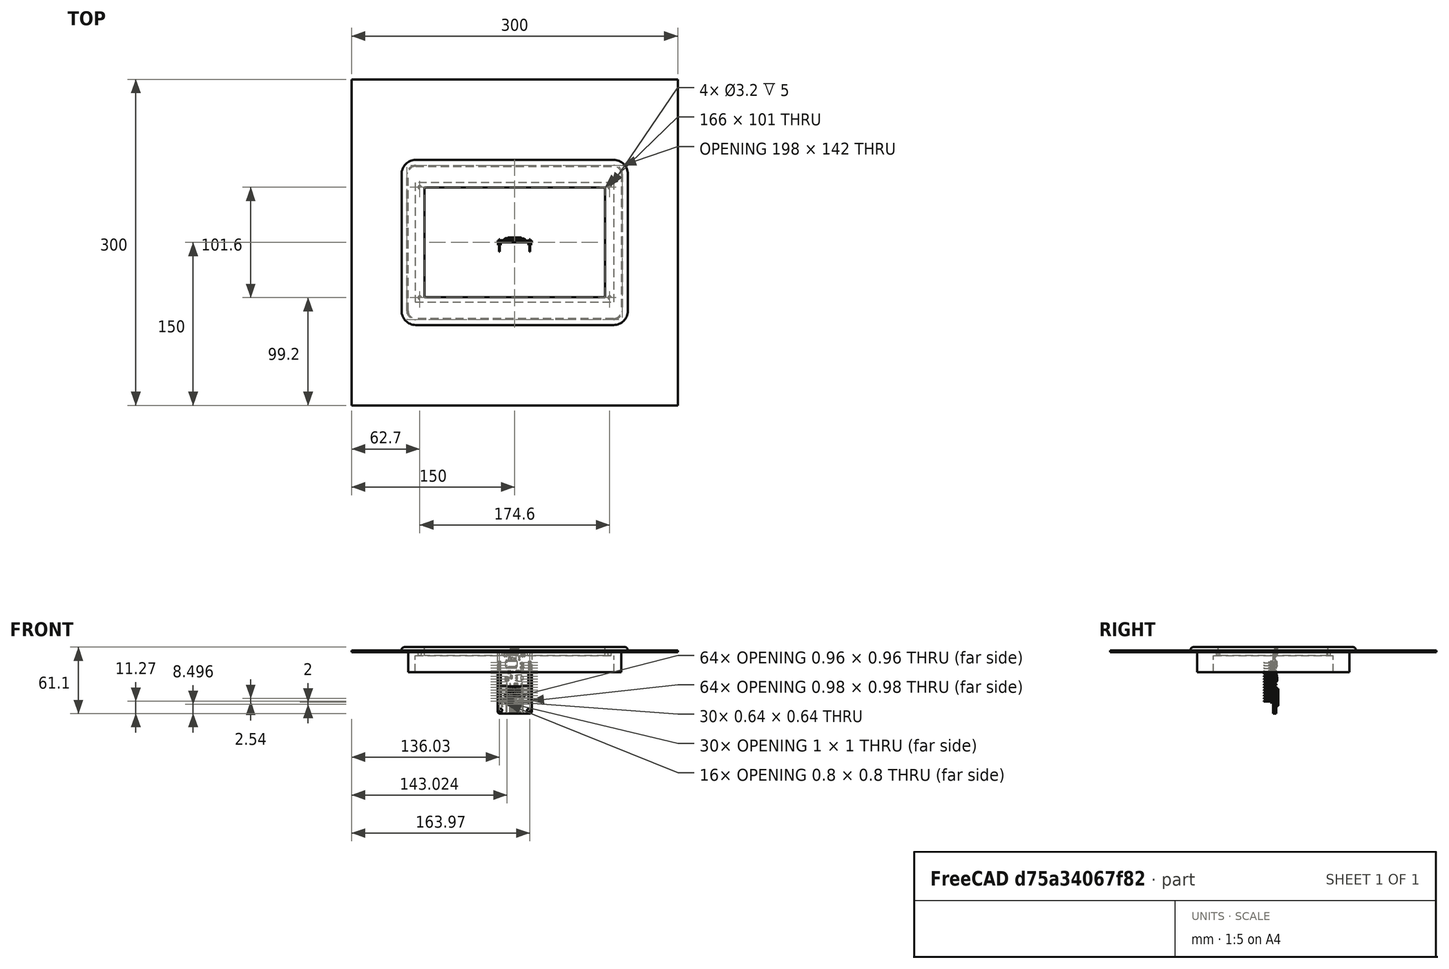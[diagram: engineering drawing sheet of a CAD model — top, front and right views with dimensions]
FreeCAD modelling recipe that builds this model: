
FCSTD DOCUMENT  (FreeCAD 0.19R21718 (Git))
Label: Marco_Respirator_2020
License: All rights reserved
LicenseURL: http://en.wikipedia.org/wiki/All_rights_reserved
objects: Sketcher::SketchObject×8, PartDesign::Pocket×4, PartDesign::Pad×3, PartDesign::Body×2, Part::Feature×2, PartDesign::Fillet×1, Mesh::Feature×1, App::Part×1
note: 28 computed .brp shape members not serialized (recipe doc carries the construction recipe); baked Part::Feature solids carry a one-line shape summary decoded from their .brp

FEATURE [Sketcher::SketchObject] Sketch
  MapMode = 5
  Support = -> [XY_Plane]
  sketch-geometry (4):
    g0: LineSegment StartX=-150 StartY=150 StartZ=0 EndX=150 EndY=150 EndZ=0
    g1: LineSegment StartX=150 StartY=150 StartZ=0 EndX=150 EndY=-150 EndZ=0
    g2: LineSegment StartX=150 StartY=-150 StartZ=0 EndX=-150 EndY=-150 EndZ=0
    g3: LineSegment StartX=-150 StartY=-150 StartZ=0 EndX=-150 EndY=150 EndZ=0
  constraints (11):
    c: Coincident(g0,g1)
    c: Coincident(g1,g2)
    c: Coincident(g2,g3)
    c: Coincident(g3,g0)
    c: Horizontal(g0)
    c: Horizontal(g2)
    c: Vertical(g1)
    c: Vertical(g3)
    c: DistanceY(g1,g1) = 300
    c: DistanceX(g2,g2) = 300
    c: Symmetric(g2,g0,g-1)
FEATURE [PartDesign::Pad] Pad
  Length = 1.5
  Length2 = 100
  Profile = -> Sketch
  Type = 0
FEATURE [Sketcher::SketchObject] Sketch001
  MapMode = 5
  Support = -> [XY_Plane]
  sketch-geometry (8):
    g0: LineSegment StartX=-91 StartY=71 StartZ=0 EndX=91 EndY=71 EndZ=0
    g1: LineSegment StartX=99 StartY=63 StartZ=0 EndX=99 EndY=-63 EndZ=0
    g2: LineSegment StartX=91 StartY=-71 StartZ=0 EndX=-91 EndY=-71 EndZ=0
    g3: LineSegment StartX=-99 StartY=-63 StartZ=0 EndX=-99 EndY=63 EndZ=0
    g4: ArcOfCircle CenterX=-91 CenterY=63 CenterZ=0 NormalX=0 NormalY=0 NormalZ=1 AngleXU=0 Radius=8 StartAngle=1.5708 EndAngle=3.14159
    g5: ArcOfCircle CenterX=91 CenterY=63 CenterZ=0 NormalX=0 NormalY=0 NormalZ=1 AngleXU=0 Radius=8 StartAngle=-5.87e-12 EndAngle=1.5708
    g6: ArcOfCircle CenterX=91 CenterY=-63 CenterZ=0 NormalX=0 NormalY=0 NormalZ=1 AngleXU=0 Radius=8 StartAngle=4.71239 EndAngle=6.28319
    g7: ArcOfCircle CenterX=-91 CenterY=-63 CenterZ=0 NormalX=0 NormalY=0 NormalZ=1 AngleXU=0 Radius=8 StartAngle=3.14159 EndAngle=4.71239
  constraints (19):
    c: Horizontal(g0)
    c: Horizontal(g2)
    c: Vertical(g1)
    c: Vertical(g3)
    c: Tangent(g3,g4) = 1.5708
    c: Tangent(g0,g4) = 1.5708
    c: Tangent(g0,g5) = 1.5708
    c: Tangent(g1,g5) = 1.5708
    c: Tangent(g1,g6) = 1.5708
    c: Tangent(g2,g6) = 1.5708
    c: Tangent(g2,g7) = 1.5708
    c: Tangent(g3,g7) = 1.5708
    c: Radius(g4) = 8
    c: Equal(g4,g5)
    c: Equal(g4,g6)
    c: Equal(g4,g7)
    c: Symmetric(g7,g5,g-1)
    c: DistanceX(g3,g1) = 198
    c: DistanceY(g2,g0) = 142
FEATURE [PartDesign::Pocket] Pocket
  BaseFeature = -> Pad
  Length = 5
  Length2 = 100
  Profile = -> Sketch001
  Reversed = true
  Type = 1
FEATURE [PartDesign::Body] Body  label="Chapa_Exterior"
  Group = -> [Sketch,Pad,Sketch001,Pocket]
  Origin = -> Origin
  Placement = pos=(0,0,-1.5) rot=(0,0,1;0rad)
  Tip = -> Pocket
FEATURE [Sketcher::SketchObject] Sketch002
  MapMode = 5
  Support = -> [XY_Plane001]
  expr: Constraints[12] = Sketch003.Constraints[12]
  expr: Constraints[17] = Sketch003.Constraints[17]
  expr: .Constraints.Ancho = Sketch003.Constraints[18]
  expr: Constraints[34] = .Constraints.Ancho + 10mm
  sketch-geometry (16):
    g0: LineSegment [constr] StartX=-91 StartY=71 StartZ=0 EndX=91 EndY=71 EndZ=0
    g1: LineSegment [constr] StartX=99 StartY=63 StartZ=0 EndX=99 EndY=-63 EndZ=0
    g2: LineSegment [constr] StartX=91 StartY=-71 StartZ=0 EndX=-91 EndY=-71 EndZ=0
    g3: LineSegment [constr] StartX=-99 StartY=-63 StartZ=0 EndX=-99 EndY=63 EndZ=0
    g4: ArcOfCircle [constr] CenterX=-91 CenterY=63 CenterZ=0 NormalX=0 NormalY=0 NormalZ=1 AngleXU=0 Radius=8 StartAngle=1.5708 EndAngle=3.14159
    g5: ArcOfCircle [constr] CenterX=91 CenterY=63 CenterZ=0 NormalX=0 NormalY=0 NormalZ=1 AngleXU=0 Radius=8 StartAngle=1e-16 EndAngle=1.5708
    g6: ArcOfCircle [constr] CenterX=91 CenterY=-63 CenterZ=0 NormalX=0 NormalY=0 NormalZ=1 AngleXU=0 Radius=8 StartAngle=4.71239 EndAngle=6.28319
    g7: ArcOfCircle [constr] CenterX=-91 CenterY=-63 CenterZ=0 NormalX=0 NormalY=0 NormalZ=1 AngleXU=0 Radius=8 StartAngle=3.14159 EndAngle=4.71239
    g8: LineSegment StartX=-91 StartY=76 StartZ=0 EndX=91 EndY=76 EndZ=0
    g9: LineSegment StartX=104 StartY=63 StartZ=0 EndX=104 EndY=-63 EndZ=0
    g10: LineSegment StartX=91 StartY=-76 StartZ=0 EndX=-91 EndY=-76 EndZ=0
    g11: LineSegment StartX=-104 StartY=-63 StartZ=0 EndX=-104 EndY=63 EndZ=0
    g12: ArcOfCircle CenterX=-91 CenterY=63 CenterZ=0 NormalX=0 NormalY=0 NormalZ=1 AngleXU=0 Radius=13 StartAngle=1.5708 EndAngle=3.14159
    g13: ArcOfCircle CenterX=91 CenterY=63 CenterZ=0 NormalX=0 NormalY=0 NormalZ=1 AngleXU=0 Radius=13 StartAngle=4e-15 EndAngle=1.5708
    g14: ArcOfCircle CenterX=91 CenterY=-63 CenterZ=0 NormalX=0 NormalY=0 NormalZ=1 AngleXU=0 Radius=13 StartAngle=4.71239 EndAngle=6.28319
    g15: ArcOfCircle CenterX=-91 CenterY=-63 CenterZ=0 NormalX=0 NormalY=0 NormalZ=1 AngleXU=0 Radius=13 StartAngle=3.14159 EndAngle=4.71239
  constraints (35):
    c: Horizontal(g0)
    c: Horizontal(g2)
    c: Vertical(g1)
    c: Vertical(g3)
    c: Tangent(g3,g4) = 1.5708
    c: Tangent(g0,g4) = 1.5708
    c: Tangent(g0,g5) = 1.5708
    c: Tangent(g1,g5) = 1.5708
    c: Tangent(g1,g6) = 1.5708
    c: Tangent(g2,g6) = 1.5708
    c: Tangent(g2,g7) = 1.5708
    c: Tangent(g3,g7) = 1.5708
    c: Radius(g4) = 8
    c: Equal(g4,g5)
    c: Equal(g4,g6)
    c: Equal(g4,g7)
    c: Symmetric(g7,g5,g-1)
    c: DistanceX(g3,g1) = 198
    c: DistanceY(g2,g0) = 142  'Ancho'
    c: Horizontal(g8)
    c: Horizontal(g10)
    c: Vertical(g9)
    c: Tangent(g11,g12) = 1.5708
    c: Tangent(g8,g12) = 1.5708
    c: Tangent(g8,g13) = 1.5708
    c: Tangent(g9,g13) = 1.5708
    c: Tangent(g9,g14) = 1.5708
    c: Tangent(g10,g14) = 1.5708
    c: Tangent(g10,g15) = 1.5708
    c: Tangent(g11,g15) = 1.5708
    c: Coincident(g12,g4)
    c: Coincident(g13,g5)
    c: Coincident(g14,g6)
    c: Coincident(g15,g7)
    c: DistanceY(g10,g8) = 152
FEATURE [Sketcher::SketchObject] Sketch003
  MapMode = 5
  Support = -> [XY_Plane001]
  sketch-geometry (8):
    g0: LineSegment StartX=-91 StartY=71 StartZ=0 EndX=91 EndY=71 EndZ=0
    g1: LineSegment StartX=99 StartY=63 StartZ=0 EndX=99 EndY=-63 EndZ=0
    g2: LineSegment StartX=91 StartY=-71 StartZ=0 EndX=-91 EndY=-71 EndZ=0
    g3: LineSegment StartX=-99 StartY=-63 StartZ=0 EndX=-99 EndY=63 EndZ=0
    g4: ArcOfCircle CenterX=-91 CenterY=63 CenterZ=0 NormalX=0 NormalY=0 NormalZ=1 AngleXU=0 Radius=8 StartAngle=1.5708 EndAngle=3.14159
    g5: ArcOfCircle CenterX=91 CenterY=63 CenterZ=0 NormalX=0 NormalY=0 NormalZ=1 AngleXU=0 Radius=8 StartAngle=-5.87e-12 EndAngle=1.5708
    g6: ArcOfCircle CenterX=91 CenterY=-63 CenterZ=0 NormalX=0 NormalY=0 NormalZ=1 AngleXU=0 Radius=8 StartAngle=4.71239 EndAngle=6.28319
    g7: ArcOfCircle CenterX=-91 CenterY=-63 CenterZ=0 NormalX=0 NormalY=0 NormalZ=1 AngleXU=0 Radius=8 StartAngle=3.14159 EndAngle=4.71239
  constraints (19):
    c: Horizontal(g0)
    c: Horizontal(g2)
    c: Vertical(g1)
    c: Vertical(g3)
    c: Tangent(g3,g4) = 1.5708
    c: Tangent(g0,g4) = 1.5708
    c: Tangent(g0,g5) = 1.5708
    c: Tangent(g1,g5) = 1.5708
    c: Tangent(g1,g6) = 1.5708
    c: Tangent(g2,g6) = 1.5708
    c: Tangent(g2,g7) = 1.5708
    c: Tangent(g3,g7) = 1.5708
    c: Radius(g4) = 8
    c: Equal(g4,g5)
    c: Equal(g4,g6)
    c: Equal(g4,g7)
    c: Symmetric(g7,g5,g-1)
    c: DistanceX(g3,g1) = 198
    c: DistanceY(g2,g0) = 142
FEATURE [PartDesign::Pad] Pad001
  Length = 3
  Length2 = 100
  Profile = -> Sketch002
  Type = 0
FEATURE [Sketcher::SketchObject] Sketch004
  MapMode = 5
  Support = -> [XY_Plane001]
  expr: Constraints[12] = Sketch003.Constraints[12]
  expr: Constraints[17] = Sketch003.Constraints[17]
  expr: .Constraints.Ancho = Sketch003.Constraints[18]
  expr: Constraints[34] = .Constraints.Ancho - 2mm
  sketch-geometry (16):
    g0: LineSegment [constr] StartX=-91 StartY=71 StartZ=0 EndX=91 EndY=71 EndZ=0
    g1: LineSegment [constr] StartX=99 StartY=63 StartZ=0 EndX=99 EndY=-63 EndZ=0
    g2: LineSegment [constr] StartX=91 StartY=-71 StartZ=0 EndX=-91 EndY=-71 EndZ=0
    g3: LineSegment [constr] StartX=-99 StartY=-63 StartZ=0 EndX=-99 EndY=63 EndZ=0
    g4: ArcOfCircle [constr] CenterX=-91 CenterY=63 CenterZ=0 NormalX=0 NormalY=0 NormalZ=1 AngleXU=0 Radius=8 StartAngle=1.5708 EndAngle=3.14159
    g5: ArcOfCircle [constr] CenterX=91 CenterY=63 CenterZ=0 NormalX=0 NormalY=0 NormalZ=1 AngleXU=0 Radius=8 StartAngle=-9e-16 EndAngle=1.5708
    g6: ArcOfCircle [constr] CenterX=91 CenterY=-63 CenterZ=0 NormalX=0 NormalY=0 NormalZ=1 AngleXU=0 Radius=8 StartAngle=4.71239 EndAngle=6.28319
    g7: ArcOfCircle [constr] CenterX=-91 CenterY=-63 CenterZ=0 NormalX=0 NormalY=0 NormalZ=1 AngleXU=0 Radius=8 StartAngle=3.14159 EndAngle=4.71239
    g8: LineSegment StartX=-91 StartY=70 StartZ=0 EndX=91 EndY=70 EndZ=0
    g9: LineSegment StartX=98 StartY=63 StartZ=0 EndX=98 EndY=-63 EndZ=0
    g10: LineSegment StartX=91 StartY=-70 StartZ=0 EndX=-91 EndY=-70 EndZ=0
    g11: LineSegment StartX=-98 StartY=-63 StartZ=0 EndX=-98 EndY=63 EndZ=0
    g12: ArcOfCircle CenterX=91 CenterY=-63 CenterZ=0 NormalX=0 NormalY=0 NormalZ=1 AngleXU=0 Radius=7 StartAngle=4.71239 EndAngle=6.28319
    g13: ArcOfCircle CenterX=-91 CenterY=-63 CenterZ=0 NormalX=0 NormalY=0 NormalZ=1 AngleXU=0 Radius=7 StartAngle=3.14159 EndAngle=4.71239
    g14: ArcOfCircle CenterX=-91 CenterY=63 CenterZ=0 NormalX=0 NormalY=0 NormalZ=1 AngleXU=0 Radius=7 StartAngle=1.5708 EndAngle=3.14159
    g15: ArcOfCircle CenterX=91 CenterY=63 CenterZ=0 NormalX=0 NormalY=0 NormalZ=1 AngleXU=0 Radius=7 StartAngle=2e-16 EndAngle=1.5708
  constraints (35):
    c: Horizontal(g0)
    c: Horizontal(g2)
    c: Vertical(g1)
    c: Vertical(g3)
    c: Tangent(g3,g4) = 1.5708
    c: Tangent(g0,g4) = 1.5708
    c: Tangent(g0,g5) = 1.5708
    c: Tangent(g1,g5) = 1.5708
    c: Tangent(g1,g6) = 1.5708
    c: Tangent(g2,g6) = 1.5708
    c: Tangent(g2,g7) = 1.5708
    c: Tangent(g3,g7) = 1.5708
    c: Radius(g4) = 8
    c: Equal(g4,g5)
    c: Equal(g4,g6)
    c: Equal(g4,g7)
    c: Symmetric(g7,g5,g-1)
    c: DistanceX(g3,g1) = 198
    c: DistanceY(g2,g0) = 142  'Ancho'
    c: Horizontal(g8)
    c: Horizontal(g10)
    c: Vertical(g9)
    c: Tangent(g9,g12) = 1.5708
    c: Tangent(g10,g12) = 1.5708
    c: Tangent(g10,g13) = 1.5708
    c: Tangent(g11,g13) = 1.5708
    c: Tangent(g8,g14) = 1.5708
    c: Tangent(g11,g14) = 1.5708
    c: Tangent(g8,g15) = 1.5708
    c: Tangent(g9,g15) = 1.5708
    c: Coincident(g15,g5)
    c: Coincident(g4,g14)
    c: Coincident(g13,g7)
    c: Coincident(g12,g6)
    c: DistanceY(g10,g8) = 140
FEATURE [PartDesign::Pad] Pad002
  BaseFeature = -> Pad001
  Length = 20
  Length2 = 100
  Profile = -> Sketch004
  Reversed = true
  Type = 0
FEATURE [PartDesign::Fillet] Fillet
  Base = -> Pad002 [Face5]
  BaseFeature = -> Pad002
  Radius = 2.5
  SupportTransform = true
FEATURE [Mesh::Feature] __0_Display  label="7.0-Display"
  Placement = pos=(-90,55,-7) rot=(1,0,0;1.5708rad)
FEATURE [Part::Feature] __0_Display001
  Placement = pos=(-0.5,-1,-5.3) rot=(0,0,1;0rad)
  shape: bbox 181 x 108 x 15.3 mm, 842 faces, 0 solids (baked)
FEATURE [Sketcher::SketchObject] Sketch005
  MapMode = 5
  Placement = pos=(0,0,-20) rot=(1,0,0;3.14159rad)
  Support = -> [Pad002]
  sketch-geometry (4):
    g0: LineSegment StartX=-83 StartY=50.5 StartZ=0 EndX=83 EndY=50.5 EndZ=0
    g1: LineSegment StartX=83 StartY=50.5 StartZ=0 EndX=83 EndY=-50.5 EndZ=0
    g2: LineSegment StartX=83 StartY=-50.5 StartZ=0 EndX=-83 EndY=-50.5 EndZ=0
    g3: LineSegment StartX=-83 StartY=-50.5 StartZ=0 EndX=-83 EndY=50.5 EndZ=0
  constraints (11):
    c: Coincident(g0,g1)
    c: Coincident(g1,g2)
    c: Coincident(g2,g3)
    c: Coincident(g3,g0)
    c: Horizontal(g0)
    c: Horizontal(g2)
    c: Vertical(g1)
    c: Vertical(g3)
    c: Symmetric(g2,g0,g-1)
    c: DistanceX(g0,g0) = 166
    c: DistanceY(g1,g1) = 101
FEATURE [PartDesign::Pocket] Pocket001
  BaseFeature = -> Fillet
  Length = 5
  Length2 = 100
  Profile = -> Sketch005
  Type = 1
FEATURE [Sketcher::SketchObject] Sketch006
  MapMode = 5
  Placement = pos=(0,0,-20) rot=(1,0,0;3.14159rad)
  Support = -> [Pocket001]
  sketch-geometry (4):
    g0: LineSegment StartX=-91.5 StartY=55 StartZ=0 EndX=91.5 EndY=55 EndZ=0
    g1: LineSegment StartX=91.5 StartY=55 StartZ=0 EndX=91.5 EndY=-55 EndZ=0
    g2: LineSegment StartX=91.5 StartY=-55 StartZ=0 EndX=-91.5 EndY=-55 EndZ=0
    g3: LineSegment StartX=-91.5 StartY=-55 StartZ=0 EndX=-91.5 EndY=55 EndZ=0
  constraints (11):
    c: Coincident(g0,g1)
    c: Coincident(g1,g2)
    c: Coincident(g2,g3)
    c: Coincident(g3,g0)
    c: Horizontal(g0)
    c: Horizontal(g2)
    c: Vertical(g1)
    c: Vertical(g3)
    c: Symmetric(g1,g0,g-1)
    c: DistanceX(g0,g0) = 183
    c: DistanceY(g1,g1) = 110
FEATURE [PartDesign::Pocket] Pocket002
  BaseFeature = -> Pocket001
  Length = 15.3
  Length2 = 100
  Profile = -> Sketch006
  Type = 0
FEATURE [Sketcher::SketchObject] Sketch007
  MapMode = 5
  Placement = pos=(0,0,-4.7) rot=(1,0,0;3.14159rad)
  Support = -> [Pocket002]
  sketch-geometry (4):
    g0: Circle CenterX=-87.3 CenterY=50.8 CenterZ=0 NormalX=0 NormalY=0 NormalZ=1 AngleXU=0 Radius=1.6
    g1: Circle CenterX=87.3 CenterY=50.8 CenterZ=0 NormalX=0 NormalY=0 NormalZ=1 AngleXU=0 Radius=1.6
    g2: Circle CenterX=87.3 CenterY=-50.8 CenterZ=0 NormalX=0 NormalY=0 NormalZ=1 AngleXU=0 Radius=1.6
    g3: Circle CenterX=-87.3 CenterY=-50.8 CenterZ=0 NormalX=0 NormalY=0 NormalZ=1 AngleXU=0 Radius=1.6
  constraints (10):
    c: Radius(g0) = 1.6
    c: DistanceX(g0,g-1) = 87.3
    c: DistanceY(g-1,g0) = 50.8
    c: Equal(g0,g1)
    c: Equal(g1,g2)
    c: Equal(g2,g3)
    c: Symmetric(g1,g0,g-2)
    c: DistanceY(g3,g-1) = 50.8
    c: DistanceX(g3,g-1) = 87.3
    c: Symmetric(g3,g2,g-2)
FEATURE [PartDesign::Pocket] Pocket003
  BaseFeature = -> Pocket002
  Length = 5
  Length2 = 100
  Profile = -> Sketch007
  Type = 0
FEATURE [PartDesign::Body] Body001  label="Marco"
  Group = -> [Sketch002,Sketch003,Pad001,Sketch004,Pad002,Fillet,Sketch005,Pocket001,Sketch006,Pocket002,Sketch007,Pocket003]
  Origin = -> Origin001
  Tip = -> Pocket003
FEATURE [App::Part] Part
  Group = -> [Body001,Body,__0_Display001]
  Origin = -> Origin002
FEATURE [Part::Feature] Feature  label="Lolin NodeMCU ESP8266 V004"
  shape: bbox 31.51 x 61.02 x 59.99 mm, 8211 faces, 260 solids (baked)
